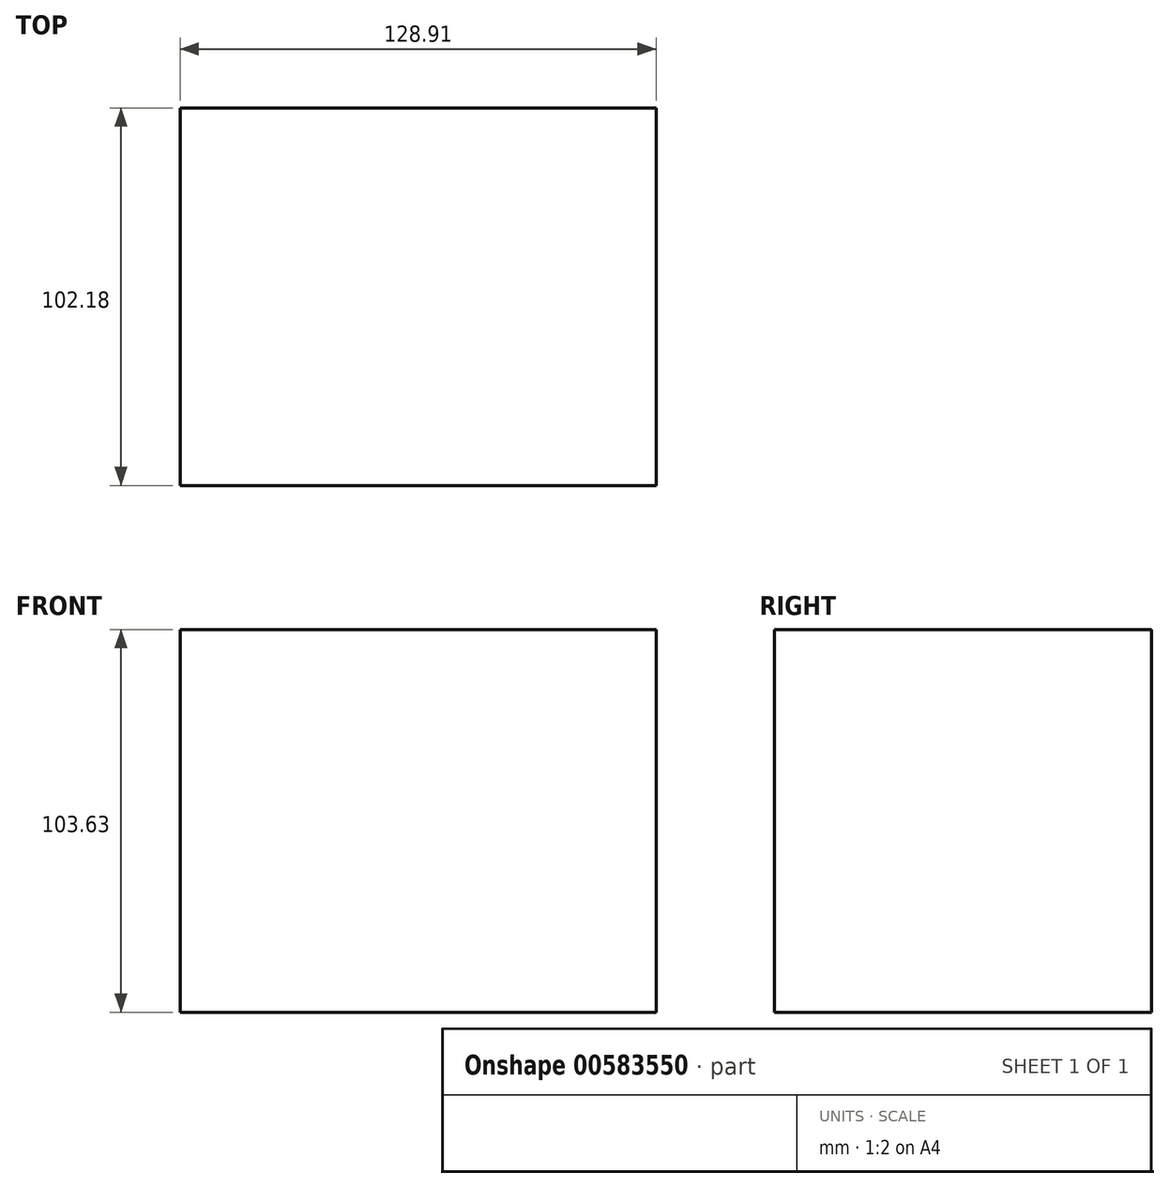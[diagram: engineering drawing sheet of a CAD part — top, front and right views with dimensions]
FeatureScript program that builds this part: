
annotation { "Feature Type Name" : "Feature", "Feature Type Description" : "" }
export const myFeature = defineFeature(function(context is Context, id is Id, definition is map)
    precondition{}
    {
        {
            var Q0;
            Q0=qCreatedBy(makeId("Top.planeOp"),FACE);
            var sketch = newSketch(context, id + "F0", { "sketchPlane" : qUnion([Q0])});
            skLineSegment(sketch, "E0.bottom", {"start": v(-64.25, 52.15) * mm, "end": v(64.66, 52.15) * mm});
            skLineSegment(sketch, "E0.top", {"start": v(-64.25, -50.03) * mm, "end": v(64.66, -50.03) * mm});
            skLineSegment(sketch, "E0.left", {"start": v(-64.25, 52.15) * mm, "end": v(-64.25, -50.03) * mm});
            skLineSegment(sketch, "E0.right", {"start": v(64.66, 52.15) * mm, "end": v(64.66, -50.03) * mm});
            skSolve(sketch);
        }
        {
            var Q0;
            Q0=makeQuery(id+"F0.imprint","IMPRINT",FACE,{"disambiguationData":[TD([[makeQuery(id+"F0.imprint","IMPRINT",EDGE,{"derivedFrom":sQuery(id+"F0.wireOp",EDGE,"E0.bottom")}),-1.0]])]});
            extrude(context, id + "F1", {"entities" : qUnion([Q0]), "depth" : 103.63 * mm, "offsetDistance" : 25.4 * mm});
        }
    });
